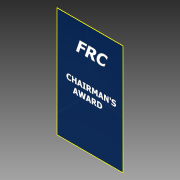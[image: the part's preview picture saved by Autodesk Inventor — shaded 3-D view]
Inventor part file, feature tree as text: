
AUTODESK INVENTOR PART (.ipt)
format: ipt  version: 2014 (Build 180170000, 170)  size: 81,920 bytes
history: native  units: in
note: dims shown in document units (in); Inventor stores cm internally (conversion verified against a paired STEP export)
features: sketch x2, extrude x1
ambient origin geometry x8: Origin, YZ Plane, XZ Plane, XY Plane, X Axis, Y Axis, Z Axis, Center Point
bodies: Solid1 (feature_tree)
feature tree (3):
  extrude  "Extrusion1"  Depth=60.0in
  sketch  "Sketch2"  dims[d2=0.2in d3=0.0in]
  sketch  "Sketch1"  dims[d0=36.0in d1=60.0in]
